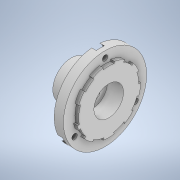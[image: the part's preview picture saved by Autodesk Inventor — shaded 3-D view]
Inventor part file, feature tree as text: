
AUTODESK INVENTOR PART (.ipt)
format: ipt  version: 2021 (Build 250183000, 183)  size: 310,272 bytes
history: native  units: mm
features: extrude x11, sketch x9, projected_geometry x4, other x3
ambient origin geometry x8: Origin, YZ Plane, XZ Plane, XY Plane, X Axis, Y Axis, Z Axis, Center Point
bodies: Solid1 (feature_tree)
feature tree (27):
  other  "wheel_gearing_mount_short.ipt"
  extrude  "Extrusion1"  Depth=10.0mm TaperAngle=0.0deg
  extrude  "Extrusion2"  Depth=10.0mm
  extrude  "Extrusion3"  Depth=13.25mm
  extrude  "Extrusion4"  Depth=10.0mm
  extrude  "Extrusion6"  Depth=7.9mm TaperAngle=0.0deg
  extrude  "Extrusion7"  Depth=10.2mm
  sketch  "Sketch9"  dims[d24=4.1mm d25=10.2mm]
  extrude  "Extrusion8"  Depth=10.0mm TaperAngle=0.0deg
  extrude  "Extrusion9"  Depth=10.0mm TaperAngle=0.0deg
  extrude  "Extrusion10"  Depth=2.5mm
  extrude  "Extrusion11"  Depth=10.0mm TaperAngle=0.0deg
  extrude  "Extrusion12"  Depth=8.0mm
  other  "Solid1::wheel_gearing_mount_short.ipt"
  other  "TaggingFeature1"
  sketch  "Sketch1"  dims[d0=10.0mm d1=10.0mm d2=0.0mm]
  projected_geometry  "Projected Loop1"
  sketch  "Sketch2"  dims[d3=10.0mm d4=0.0mm d5=20.0mm]
  projected_geometry  "Projected Loop2"
  sketch  "Sketch3"  dims[d6=13.25mm d7=0.0mm d8=12.2mm]
  sketch  "Sketch4"  dims[d9=10.75mm d10=0.0mm d16=10.0mm]
  sketch  "Sketch6"  dims[d17=11.5mm d18=0.0mm d21=7.9mm d22=0.0mm]
  projected_geometry  "Projected Loop3"
  projected_geometry  "Projected Loop4"
  sketch  "Sketch10"  dims[d26=10.0mm d27=0.0mm d28=10.0mm d29=0.0mm]
  sketch  "Sketch11"  dims[d30=16.0mm d31=10.0mm d32=0.0mm]
  sketch  "Sketch12"  dims[d33=0.1mm d34=0.1mm d35=10.0mm d36=0.0mm d37=8.0mm d38=8.0mm d39=8.0mm d40=2.5mm d41=0.0mm]
